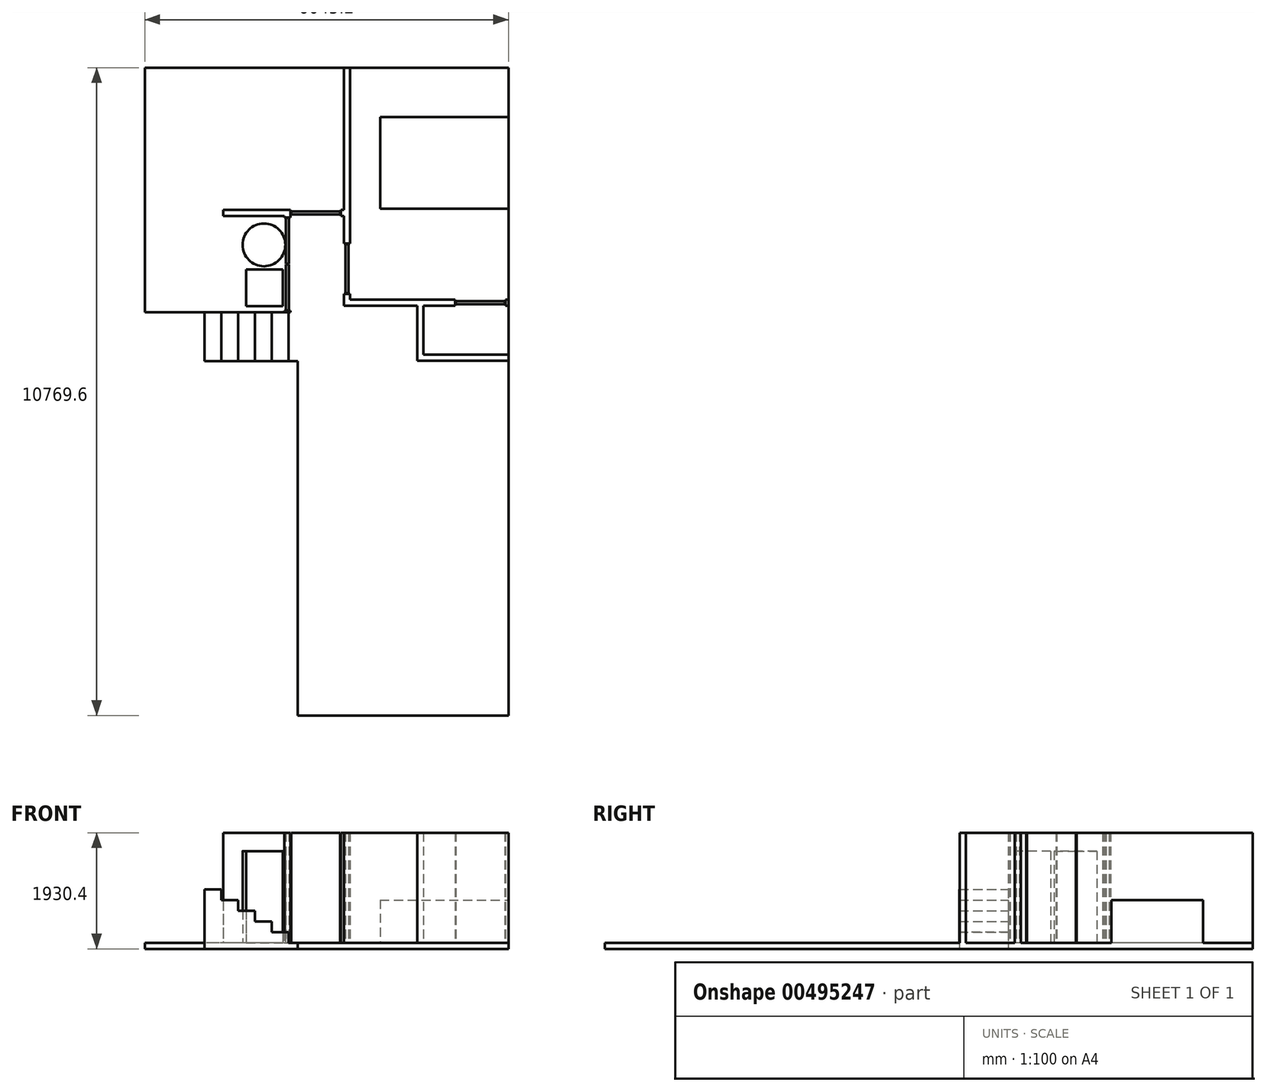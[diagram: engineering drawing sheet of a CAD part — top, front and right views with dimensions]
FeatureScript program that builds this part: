
annotation { "Feature Type Name" : "Feature", "Feature Type Description" : "" }
export const myFeature = defineFeature(function(context is Context, id is Id, definition is map)
    precondition{}
    {
        {
            var Q0;
            Q0=qCreatedBy(makeId("Top.planeOp"),FACE);
            var sketch = newSketch(context, id + "F0", { "sketchPlane" : qUnion([Q0])});
            skLineSegment(sketch, "E0.bottom", {"start": v(0, 0) * mm, "end": v(-6045.2, 0) * mm});
            skLineSegment(sketch, "E0.top", {"start": v(-3657.6, -4064) * mm, "end": v(-6045.2, -4064) * mm});
            skLineSegment(sketch, "E0.left", {"start": v(0, 0) * mm, "end": v(0, -4064) * mm});
            skLineSegment(sketch, "E0.right", {"start": v(-6045.2, 0) * mm, "end": v(-6045.2, -4064) * mm});
            skLineSegment(sketch, "E1.top", {"start": v(-3505.2, -10769.6) * mm, "end": v(0, -10769.6) * mm});
            skLineSegment(sketch, "E1.left", {"start": v(-3505.2, -4876.8) * mm, "end": v(-3505.2, -10769.6) * mm});
            skLineSegment(sketch, "E1.right", {"start": v(0, -4064) * mm, "end": v(0, -10769.6) * mm});
            skLineSegment(sketch, "E2.top", {"start": v(-3657.6, -4876.8) * mm, "end": v(-3505.2, -4876.8) * mm});
            skLineSegment(sketch, "E2.left", {"start": v(-3657.6, -4064) * mm, "end": v(-3657.6, -4876.8) * mm});
            skSolve(sketch);
        }
        {
            var Q0;
            Q0 = qSketchRegion(id + "F0", true);
            extrude(context, id + "F1", {"entities" : qUnion([Q0]), "depth" : 101.6 * mm});
        }
        {
            var Q0;
            Q0=makeQuery(id+"F1.opExtrude","CAP_FACE",FACE,{"disambiguationData":[OSD([sQuery(id+"F0.wireOp",EDGE,"E0.bottom"),sQuery(id+"F0.wireOp",EDGE,"E0.top"),sQuery(id+"F0.wireOp",EDGE,"E0.left"),sQuery(id+"F0.wireOp",EDGE,"E0.right"),sQuery(id+"F0.wireOp",EDGE,"E1.top"),sQuery(id+"F0.wireOp",EDGE,"E1.left"),sQuery(id+"F0.wireOp",EDGE,"E1.right")])],"isStart":false});
            var sketch = newSketch(context, id + "F2", { "sketchPlane" : qUnion([Q0])});
            skCircle(sketch, "E3", {"center": v(-4064, -2946.4) * mm, "radius": 355.6 * mm});
            skLineSegment(sketch, "E4.bottom", {"start": v(-4358.58, -3355.94) * mm, "end": v(-3748.98, -3355.94) * mm});
            skLineSegment(sketch, "E4.top", {"start": v(-4358.58, -3965.54) * mm, "end": v(-3748.98, -3965.54) * mm});
            skLineSegment(sketch, "E4.left", {"start": v(-4358.58, -3355.94) * mm, "end": v(-4358.58, -3965.54) * mm});
            skLineSegment(sketch, "E4.right", {"start": v(-3748.98, -3355.94) * mm, "end": v(-3748.98, -3965.54) * mm});
            skSolve(sketch);
        }
        {
            var Q0;
            Q0 = qSketchRegion(id + "F2", true);
            extrude(context, id + "F3", {"entities" : qUnion([Q0]), "operationType" : NewBodyOperationType.ADD, "depth" : 1524 * mm});
        }
        {
            var Q0;
            Q0=makeQuery(id+"F1.opExtrude","CAP_FACE",FACE,{"disambiguationData":[OSD([sQuery(id+"F0.wireOp",EDGE,"E0.bottom"),sQuery(id+"F0.wireOp",EDGE,"E0.top"),sQuery(id+"F0.wireOp",EDGE,"E0.left"),sQuery(id+"F0.wireOp",EDGE,"E0.right"),sQuery(id+"F0.wireOp",EDGE,"E1.top"),sQuery(id+"F0.wireOp",EDGE,"E1.left"),sQuery(id+"F0.wireOp",EDGE,"E1.right")])],"isStart":false});
            var sketch = newSketch(context, id + "F4", { "sketchPlane" : qUnion([Q0])});
            skLineSegment(sketch, "E5.bottom", {"start": v(-3621.98, -4064) * mm, "end": v(-3723.58, -4064) * mm});
            skLineSegment(sketch, "E5.top", {"start": v(-3621.98, -4038.6) * mm, "end": v(-3723.58, -4038.6) * mm});
            skLineSegment(sketch, "E5.left", {"start": v(-3621.98, -4064) * mm, "end": v(-3621.98, -4038.6) * mm});
            skLineSegment(sketch, "E5.right", {"start": v(-3723.58, -4064) * mm, "end": v(-3723.58, -4038.6) * mm});
            skLineSegment(sketch, "E6.bottom", {"start": v(-3698.18, -3270.25) * mm, "end": v(-3647.38, -3270.25) * mm});
            skLineSegment(sketch, "E6.top", {"start": v(-3698.18, -4032.25) * mm, "end": v(-3647.38, -4032.25) * mm});
            skLineSegment(sketch, "E6.left", {"start": v(-3698.18, -3270.25) * mm, "end": v(-3698.18, -4032.25) * mm});
            skLineSegment(sketch, "E6.right", {"start": v(-3647.38, -3270.25) * mm, "end": v(-3647.38, -4032.25) * mm});
            skLineSegment(sketch, "E7.bottom", {"start": v(-3698.18, -3257.55) * mm, "end": v(-3647.38, -3257.55) * mm});
            skLineSegment(sketch, "E7.top", {"start": v(-3698.18, -2495.55) * mm, "end": v(-3647.38, -2495.55) * mm});
            skLineSegment(sketch, "E7.left", {"start": v(-3698.18, -3257.55) * mm, "end": v(-3698.18, -2495.55) * mm});
            skLineSegment(sketch, "E7.right", {"start": v(-3647.38, -3257.55) * mm, "end": v(-3647.38, -2495.55) * mm});
            skLineSegment(sketch, "E8.top", {"start": v(-3723.58, -2489.2) * mm, "end": v(-3621.98, -2489.2) * mm});
            skLineSegment(sketch, "E8.left", {"start": v(-3723.58, -2463.8) * mm, "end": v(-3723.58, -2489.2) * mm});
            skLineSegment(sketch, "E8.right", {"start": v(-3621.98, -2463.8) * mm, "end": v(-3621.98, -2489.2) * mm});
            skLineSegment(sketch, "E9.bottom", {"start": v(-3723.58, -2463.8) * mm, "end": v(-4739.58, -2463.8) * mm});
            skLineSegment(sketch, "E9.top", {"start": v(-3621.98, -2362.2) * mm, "end": v(-4739.58, -2362.2) * mm});
            skLineSegment(sketch, "E9.left", {"start": v(-3621.98, -2463.8) * mm, "end": v(-3621.98, -2362.2) * mm});
            skLineSegment(sketch, "E9.right", {"start": v(-4739.58, -2463.8) * mm, "end": v(-4739.58, -2362.2) * mm});
            skLineSegment(sketch, "E10.bottom", {"start": v(-2631.38, 0) * mm, "end": v(-2732.98, 0) * mm});
            skLineSegment(sketch, "E10.left", {"start": v(-2631.38, 0) * mm, "end": v(-2631.38, -2925.52) * mm});
            skLineSegment(sketch, "E10.right", {"start": v(-2732.98, 0) * mm, "end": v(-2732.98, -2925.52) * mm});
            skLineSegment(sketch, "E11.bottom", {"start": v(-2631.38, -3854.56) * mm, "end": v(-889, -3854.56) * mm});
            skLineSegment(sketch, "E11.top", {"start": v(-2732.98, -3956.16) * mm, "end": v(-1513.78, -3956.16) * mm});
            skLineSegment(sketch, "E11.left", {"start": v(-2732.98, -3854.56) * mm, "end": v(-2732.98, -3956.16) * mm});
            skLineSegment(sketch, "E11.right", {"start": v(0, -3854.56) * mm, "end": v(0, -3956.16) * mm});
            skLineSegment(sketch, "E12.bottom", {"start": v(-2732.98, -2362.2) * mm, "end": v(-2783.78, -2362.2) * mm});
            skLineSegment(sketch, "E12.top", {"start": v(-2732.98, -2463.8) * mm, "end": v(-2783.78, -2463.8) * mm});
            skLineSegment(sketch, "E12.left", {"start": v(-2732.98, -2362.2) * mm, "end": v(-2732.98, -2463.8) * mm});
            skLineSegment(sketch, "E12.right", {"start": v(-2783.78, -2362.2) * mm, "end": v(-2783.78, -2463.8) * mm});
            skLineSegment(sketch, "E13.bottom", {"start": v(-3609.28, -2387.6) * mm, "end": v(-2796.48, -2387.6) * mm});
            skLineSegment(sketch, "E13.top", {"start": v(-3609.28, -2438.4) * mm, "end": v(-2796.48, -2438.4) * mm});
            skLineSegment(sketch, "E13.left", {"start": v(-3609.28, -2387.6) * mm, "end": v(-3609.28, -2438.4) * mm});
            skLineSegment(sketch, "E13.right", {"start": v(-2796.48, -2387.6) * mm, "end": v(-2796.48, -2438.4) * mm});
            skLineSegment(sketch, "E14.bottom", {"start": v(-2732.98, -2925.52) * mm, "end": v(-2631.38, -2925.52) * mm});
            skLineSegment(sketch, "E14.top", {"start": v(-2732.98, -3763.72) * mm, "end": v(-2631.38, -3763.72) * mm});
            skLineSegment(sketch, "E15.trimOffspring", {"start": v(-2732.98, -3763.72) * mm, "end": v(-2732.98, -3854.56) * mm});
            skLineSegment(sketch, "E16.trimOffspring", {"start": v(-2631.38, -3763.72) * mm, "end": v(-2631.38, -3854.56) * mm});
            skLineSegment(sketch, "E17.bottom", {"start": v(-2707.58, -3751.02) * mm, "end": v(-2656.78, -3751.02) * mm});
            skLineSegment(sketch, "E17.top", {"start": v(-2707.58, -2938.22) * mm, "end": v(-2656.78, -2938.22) * mm});
            skLineSegment(sketch, "E17.left", {"start": v(-2707.58, -3751.02) * mm, "end": v(-2707.58, -2938.22) * mm});
            skLineSegment(sketch, "E17.right", {"start": v(-2656.78, -3751.02) * mm, "end": v(-2656.78, -2938.22) * mm});
            skLineSegment(sketch, "E18.left", {"start": v(-50.8, -3854.56) * mm, "end": v(-50.8, -3956.16) * mm});
            skLineSegment(sketch, "E18.right", {"start": v(-889, -3854.56) * mm, "end": v(-889, -3956.16) * mm});
            skLineSegment(sketch, "E19.trimOffspring", {"start": v(-50.8, -3956.16) * mm, "end": v(0, -3956.16) * mm});
            skLineSegment(sketch, "E20.trimOffspring", {"start": v(-50.8, -3854.56) * mm, "end": v(0, -3854.56) * mm});
            skLineSegment(sketch, "E21.bottom", {"start": v(-876.3, -3879.96) * mm, "end": v(-63.5, -3879.96) * mm});
            skLineSegment(sketch, "E21.top", {"start": v(-876.3, -3930.76) * mm, "end": v(-63.5, -3930.76) * mm});
            skLineSegment(sketch, "E21.left", {"start": v(-876.3, -3879.96) * mm, "end": v(-876.3, -3930.76) * mm});
            skLineSegment(sketch, "E21.right", {"start": v(-63.5, -3879.96) * mm, "end": v(-63.5, -3930.76) * mm});
            skLineSegment(sketch, "E22.top", {"start": v(-1513.78, -4870.56) * mm, "end": v(-1412.18, -4870.56) * mm});
            skLineSegment(sketch, "E22.left", {"start": v(-1513.78, -3956.16) * mm, "end": v(-1513.78, -4870.56) * mm});
            skLineSegment(sketch, "E22.right", {"start": v(-1412.18, -3956.16) * mm, "end": v(-1412.18, -4768.96) * mm});
            skLineSegment(sketch, "E23.bottom", {"start": v(-1412.18, -4870.56) * mm, "end": v(0, -4870.56) * mm});
            skLineSegment(sketch, "E23.top", {"start": v(-1412.18, -4768.96) * mm, "end": v(0, -4768.96) * mm});
            skLineSegment(sketch, "E23.right", {"start": v(0, -4870.56) * mm, "end": v(0, -4768.96) * mm});
            skLineSegment(sketch, "E24.trimOffspring", {"start": v(-1412.18, -3956.16) * mm, "end": v(-889, -3956.16) * mm});
            skSolve(sketch);
        }
        {
            var Q0;
            Q0 = qSketchRegion(id + "F4", true);
            extrude(context, id + "F5", {"entities" : qUnion([Q0]), "operationType" : NewBodyOperationType.ADD, "depth" : 1828.8 * mm});
        }
        {
            var Q0;
            Q0=makeQuery(id+"F1.opExtrude","CAP_FACE",FACE,{"disambiguationData":[OSD([sQuery(id+"F0.wireOp",EDGE,"E0.bottom"),sQuery(id+"F0.wireOp",EDGE,"E0.top"),sQuery(id+"F0.wireOp",EDGE,"E0.left"),sQuery(id+"F0.wireOp",EDGE,"E0.right"),sQuery(id+"F0.wireOp",EDGE,"E1.top"),sQuery(id+"F0.wireOp",EDGE,"E1.left"),sQuery(id+"F0.wireOp",EDGE,"E1.right"),sQuery(id+"F0.wireOp",EDGE,"E2.top"),sQuery(id+"F0.wireOp",EDGE,"E2.left")])],"isStart":true});
            var sketch = newSketch(context, id + "F6", { "sketchPlane" : qUnion([Q0])});
            skLineSegment(sketch, "E25.bottom", {"start": v(-3657.6, 4876.8) * mm, "end": v(-3937, 4876.8) * mm});
            skLineSegment(sketch, "E25.top", {"start": v(-3657.6, 4064) * mm, "end": v(-3937, 4064) * mm});
            skLineSegment(sketch, "E25.left", {"start": v(-3657.6, 4876.8) * mm, "end": v(-3657.6, 4064) * mm});
            skLineSegment(sketch, "E25.right", {"start": v(-3937, 4876.8) * mm, "end": v(-3937, 4064) * mm});
            skSolve(sketch);
        }
        {
            var Q0;
            Q0 = qSketchRegion(id + "F6", true);
            extrude(context, id + "F7", {"entities" : qUnion([Q0]), "operationType" : NewBodyOperationType.ADD, "oppositeDirection" : true, "depth" : 279.4 * mm});
        }
        {
            var Q0;
            Q0=makeQuery(id+"F7.boolean.opBoolean","MERGE",FACE,{"derivedFrom":[makeQuery(id+"F1.opExtrude","CAP_FACE",FACE,{"disambiguationData":[OSD([sQuery(id+"F0.wireOp",EDGE,"E0.bottom"),sQuery(id+"F0.wireOp",EDGE,"E0.top"),sQuery(id+"F0.wireOp",EDGE,"E0.left"),sQuery(id+"F0.wireOp",EDGE,"E0.right"),sQuery(id+"F0.wireOp",EDGE,"E1.top"),sQuery(id+"F0.wireOp",EDGE,"E1.left"),sQuery(id+"F0.wireOp",EDGE,"E1.right"),sQuery(id+"F0.wireOp",EDGE,"E2.top"),sQuery(id+"F0.wireOp",EDGE,"E2.left")])],"isStart":true}),makeQuery(id+"F7.opExtrude","CAP_FACE",FACE,{"disambiguationData":[OSD([sQuery(id+"F6.wireOp",EDGE,"E25.bottom"),sQuery(id+"F6.wireOp",EDGE,"E25.top"),sQuery(id+"F6.wireOp",EDGE,"E25.left"),sQuery(id+"F6.wireOp",EDGE,"E25.right")])],"isStart":true})]});
            var sketch = newSketch(context, id + "F8", { "sketchPlane" : qUnion([Q0])});
            skLineSegment(sketch, "E26.bottom", {"start": v(-3937, 4876.8) * mm, "end": v(-4216.4, 4876.8) * mm});
            skLineSegment(sketch, "E26.top", {"start": v(-3937, 4064) * mm, "end": v(-4216.4, 4064) * mm});
            skLineSegment(sketch, "E26.left", {"start": v(-3937, 4876.8) * mm, "end": v(-3937, 4064) * mm});
            skLineSegment(sketch, "E26.right", {"start": v(-4216.4, 4876.8) * mm, "end": v(-4216.4, 4064) * mm});
            skSolve(sketch);
        }
        {
            var Q0;
            Q0 = qSketchRegion(id + "F8", true);
            extrude(context, id + "F9", {"entities" : qUnion([Q0]), "operationType" : NewBodyOperationType.ADD, "oppositeDirection" : true, "depth" : 457.2 * mm});
        }
        {
            var Q0;
            Q0=makeQuery(id+"F9.boolean.opBoolean","MERGE",FACE,{"derivedFrom":[makeQuery(id+"F7.boolean.opBoolean","MERGE",FACE,{"derivedFrom":[makeQuery(id+"F1.opExtrude","CAP_FACE",FACE,{"disambiguationData":[OSD([sQuery(id+"F0.wireOp",EDGE,"E0.bottom"),sQuery(id+"F0.wireOp",EDGE,"E0.top"),sQuery(id+"F0.wireOp",EDGE,"E0.left"),sQuery(id+"F0.wireOp",EDGE,"E0.right"),sQuery(id+"F0.wireOp",EDGE,"E1.top"),sQuery(id+"F0.wireOp",EDGE,"E1.left"),sQuery(id+"F0.wireOp",EDGE,"E1.right"),sQuery(id+"F0.wireOp",EDGE,"E2.top"),sQuery(id+"F0.wireOp",EDGE,"E2.left")])],"isStart":true}),makeQuery(id+"F7.opExtrude","CAP_FACE",FACE,{"disambiguationData":[OSD([sQuery(id+"F6.wireOp",EDGE,"E25.bottom"),sQuery(id+"F6.wireOp",EDGE,"E25.top"),sQuery(id+"F6.wireOp",EDGE,"E25.left"),sQuery(id+"F6.wireOp",EDGE,"E25.right")])],"isStart":true})]}),makeQuery(id+"F9.opExtrude","CAP_FACE",FACE,{"disambiguationData":[OSD([sQuery(id+"F8.wireOp",EDGE,"E26.bottom"),sQuery(id+"F8.wireOp",EDGE,"E26.top"),sQuery(id+"F8.wireOp",EDGE,"E26.left"),sQuery(id+"F8.wireOp",EDGE,"E26.right")])],"isStart":true})]});
            var sketch = newSketch(context, id + "F10", { "sketchPlane" : qUnion([Q0])});
            skLineSegment(sketch, "E27.bottom", {"start": v(-4216.4, 4876.8) * mm, "end": v(-4495.8, 4876.8) * mm});
            skLineSegment(sketch, "E27.top", {"start": v(-4216.4, 4064) * mm, "end": v(-4495.8, 4064) * mm});
            skLineSegment(sketch, "E27.left", {"start": v(-4216.4, 4876.8) * mm, "end": v(-4216.4, 4064) * mm});
            skLineSegment(sketch, "E27.right", {"start": v(-4495.8, 4876.8) * mm, "end": v(-4495.8, 4064) * mm});
            skSolve(sketch);
        }
        {
            var Q0;
            Q0 = qSketchRegion(id + "F10", true);
            extrude(context, id + "F11", {"entities" : qUnion([Q0]), "operationType" : NewBodyOperationType.ADD, "oppositeDirection" : true, "depth" : 635 * mm});
        }
        {
            var Q0;
            Q0=makeQuery(id+"F11.boolean.opBoolean","MERGE",FACE,{"derivedFrom":[makeQuery(id+"F9.boolean.opBoolean","MERGE",FACE,{"derivedFrom":[makeQuery(id+"F7.boolean.opBoolean","MERGE",FACE,{"derivedFrom":[makeQuery(id+"F1.opExtrude","CAP_FACE",FACE,{"disambiguationData":[OSD([sQuery(id+"F0.wireOp",EDGE,"E0.bottom"),sQuery(id+"F0.wireOp",EDGE,"E0.top"),sQuery(id+"F0.wireOp",EDGE,"E0.left"),sQuery(id+"F0.wireOp",EDGE,"E0.right"),sQuery(id+"F0.wireOp",EDGE,"E1.top"),sQuery(id+"F0.wireOp",EDGE,"E1.left"),sQuery(id+"F0.wireOp",EDGE,"E1.right"),sQuery(id+"F0.wireOp",EDGE,"E2.top"),sQuery(id+"F0.wireOp",EDGE,"E2.left")])],"isStart":true}),makeQuery(id+"F7.opExtrude","CAP_FACE",FACE,{"disambiguationData":[OSD([sQuery(id+"F6.wireOp",EDGE,"E25.bottom"),sQuery(id+"F6.wireOp",EDGE,"E25.top"),sQuery(id+"F6.wireOp",EDGE,"E25.left"),sQuery(id+"F6.wireOp",EDGE,"E25.right")])],"isStart":true})]}),makeQuery(id+"F9.opExtrude","CAP_FACE",FACE,{"disambiguationData":[OSD([sQuery(id+"F8.wireOp",EDGE,"E26.bottom"),sQuery(id+"F8.wireOp",EDGE,"E26.top"),sQuery(id+"F8.wireOp",EDGE,"E26.left"),sQuery(id+"F8.wireOp",EDGE,"E26.right")])],"isStart":true})]}),makeQuery(id+"F11.opExtrude","CAP_FACE",FACE,{"disambiguationData":[OSD([sQuery(id+"F10.wireOp",EDGE,"E27.bottom"),sQuery(id+"F10.wireOp",EDGE,"E27.top"),sQuery(id+"F10.wireOp",EDGE,"E27.left"),sQuery(id+"F10.wireOp",EDGE,"E27.right")])],"isStart":true})]});
            var sketch = newSketch(context, id + "F12", { "sketchPlane" : qUnion([Q0])});
            skLineSegment(sketch, "E28.bottom", {"start": v(-4495.8, 4876.8) * mm, "end": v(-4775.2, 4876.8) * mm});
            skLineSegment(sketch, "E28.top", {"start": v(-4495.8, 4064) * mm, "end": v(-4775.2, 4064) * mm});
            skLineSegment(sketch, "E28.left", {"start": v(-4495.8, 4876.8) * mm, "end": v(-4495.8, 4064) * mm});
            skLineSegment(sketch, "E28.right", {"start": v(-4775.2, 4876.8) * mm, "end": v(-4775.2, 4064) * mm});
            skSolve(sketch);
        }
        {
            var Q0;
            Q0 = qSketchRegion(id + "F12", true);
            extrude(context, id + "F13", {"entities" : qUnion([Q0]), "operationType" : NewBodyOperationType.ADD, "oppositeDirection" : true, "depth" : 812.8 * mm});
        }
        {
            var Q0;
            Q0=makeQuery(id+"F13.boolean.opBoolean","MERGE",FACE,{"derivedFrom":[makeQuery(id+"F11.boolean.opBoolean","MERGE",FACE,{"derivedFrom":[makeQuery(id+"F9.boolean.opBoolean","MERGE",FACE,{"derivedFrom":[makeQuery(id+"F7.boolean.opBoolean","MERGE",FACE,{"derivedFrom":[makeQuery(id+"F1.opExtrude","CAP_FACE",FACE,{"disambiguationData":[OSD([sQuery(id+"F0.wireOp",EDGE,"E0.bottom"),sQuery(id+"F0.wireOp",EDGE,"E0.top"),sQuery(id+"F0.wireOp",EDGE,"E0.left"),sQuery(id+"F0.wireOp",EDGE,"E0.right"),sQuery(id+"F0.wireOp",EDGE,"E1.top"),sQuery(id+"F0.wireOp",EDGE,"E1.left"),sQuery(id+"F0.wireOp",EDGE,"E1.right"),sQuery(id+"F0.wireOp",EDGE,"E2.top"),sQuery(id+"F0.wireOp",EDGE,"E2.left")])],"isStart":true}),makeQuery(id+"F7.opExtrude","CAP_FACE",FACE,{"disambiguationData":[OSD([sQuery(id+"F6.wireOp",EDGE,"E25.bottom"),sQuery(id+"F6.wireOp",EDGE,"E25.top"),sQuery(id+"F6.wireOp",EDGE,"E25.left"),sQuery(id+"F6.wireOp",EDGE,"E25.right")])],"isStart":true})]}),makeQuery(id+"F9.opExtrude","CAP_FACE",FACE,{"disambiguationData":[OSD([sQuery(id+"F8.wireOp",EDGE,"E26.bottom"),sQuery(id+"F8.wireOp",EDGE,"E26.top"),sQuery(id+"F8.wireOp",EDGE,"E26.left"),sQuery(id+"F8.wireOp",EDGE,"E26.right")])],"isStart":true})]}),makeQuery(id+"F11.opExtrude","CAP_FACE",FACE,{"disambiguationData":[OSD([sQuery(id+"F10.wireOp",EDGE,"E27.bottom"),sQuery(id+"F10.wireOp",EDGE,"E27.top"),sQuery(id+"F10.wireOp",EDGE,"E27.left"),sQuery(id+"F10.wireOp",EDGE,"E27.right")])],"isStart":true})]}),makeQuery(id+"F13.opExtrude","CAP_FACE",FACE,{"disambiguationData":[OSD([sQuery(id+"F12.wireOp",EDGE,"E28.bottom"),sQuery(id+"F12.wireOp",EDGE,"E28.top"),sQuery(id+"F12.wireOp",EDGE,"E28.left"),sQuery(id+"F12.wireOp",EDGE,"E28.right")])],"isStart":true})]});
            var sketch = newSketch(context, id + "F14", { "sketchPlane" : qUnion([Q0])});
            skLineSegment(sketch, "E29.bottom", {"start": v(-4775.2, 4876.8) * mm, "end": v(-5054.6, 4876.8) * mm});
            skLineSegment(sketch, "E29.top", {"start": v(-4775.2, 4064) * mm, "end": v(-5054.6, 4064) * mm});
            skLineSegment(sketch, "E29.left", {"start": v(-4775.2, 4876.8) * mm, "end": v(-4775.2, 4064) * mm});
            skLineSegment(sketch, "E29.right", {"start": v(-5054.6, 4876.8) * mm, "end": v(-5054.6, 4064) * mm});
            skSolve(sketch);
        }
        {
            var Q0;
            Q0 = qSketchRegion(id + "F14", true);
            extrude(context, id + "F15", {"entities" : qUnion([Q0]), "operationType" : NewBodyOperationType.ADD, "oppositeDirection" : true, "depth" : 990.6 * mm});
        }
        {
            var Q0;
            Q0=makeQuery(id+"F1.opExtrude","CAP_FACE",FACE,{"disambiguationData":[OSD([sQuery(id+"F0.wireOp",EDGE,"E0.bottom"),sQuery(id+"F0.wireOp",EDGE,"E0.top"),sQuery(id+"F0.wireOp",EDGE,"E0.left"),sQuery(id+"F0.wireOp",EDGE,"E0.right"),sQuery(id+"F0.wireOp",EDGE,"E1.top"),sQuery(id+"F0.wireOp",EDGE,"E1.left"),sQuery(id+"F0.wireOp",EDGE,"E1.right"),sQuery(id+"F0.wireOp",EDGE,"E2.top"),sQuery(id+"F0.wireOp",EDGE,"E2.left")])],"isStart":false});
            var sketch = newSketch(context, id + "F16", { "sketchPlane" : qUnion([Q0])});
            skLineSegment(sketch, "E30.bottom", {"start": v(-2133.6, -824.67) * mm, "end": v(0, -824.67) * mm});
            skLineSegment(sketch, "E30.top", {"start": v(-2133.6, -2348.67) * mm, "end": v(0, -2348.67) * mm});
            skLineSegment(sketch, "E30.left", {"start": v(-2133.6, -824.67) * mm, "end": v(-2133.6, -2348.67) * mm});
            skLineSegment(sketch, "E30.right", {"start": v(0, -824.67) * mm, "end": v(0, -2348.67) * mm});
            skSolve(sketch);
        }
        {
            var Q0;
            Q0 = qSketchRegion(id + "F16", true);
            extrude(context, id + "F17", {"entities" : qUnion([Q0]), "operationType" : NewBodyOperationType.ADD, "depth" : 711.2 * mm});
        }
    });
